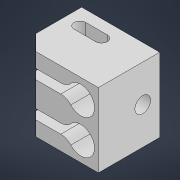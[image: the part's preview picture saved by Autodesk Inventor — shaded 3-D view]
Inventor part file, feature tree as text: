
AUTODESK INVENTOR PART (.ipt)
format: ipt  version: 2022 (Build 260153000, 153)  size: 290,304 bytes
history: native  units: in
note: dims shown in document units (in); Inventor stores cm internally (conversion verified against a paired STEP export)
features: sketch x14, extrude x8, plane x3, chamfer x3, projected_geometry x3, mirror x1
ambient origin geometry x8: Origin, YZ Plane, XZ Plane, XY Plane, X Axis, Y Axis, Z Axis, Center Point
bodies: Solid5 (feature_tree)
feature tree (32):
  plane  "Work Plane1"
  plane  "Work Plane2"
  sketch  "Sketch12"  dims[d38=0.1378in]
  extrude  "Extrusion15"  Depth=0.6693in TaperAngle=0.0deg
  extrude  "Extrusion16"  Depth=0.0984in TaperAngle=0.0deg
  chamfer  "Chamfer1"  Distance=0.2756in
  chamfer  "Chamfer2"  Distance=0.3937in
  extrude  "Extrusion18"  Depth=0.0787in
  chamfer  "Chamfer4"  Distance=0.3937in
  plane  "Work Plane3"
  extrude  "Extrusion19"  Depth=0.0787in TaperAngle=45.0deg
  mirror  "Mirror1"
  extrude  "Extrusion20"  Depth=0.0787in TaperAngle=45.0deg
  extrude  "Extrusion22"  Depth=0.0787in TaperAngle=45.0deg
  extrude  "Extrusion23"  Depth=0.0787in
  extrude  "Extrusion24"  Depth=0.3937in TaperAngle=0.0deg
  sketch  "Sketch1"  dims[d0=1.2997in d1=0.6693in d2=0.0in]
  sketch  "Sketch2"  dims[d3=0.2756in d4=0.0in d5=0.0984in d6=0.0in d7=0.2756in d8=-0.0in]
  sketch  "Sketch3"  dims[d9=0.7579in d12=0.3937in d13=0.0in]
  sketch  "Sketch4"  dims[d14=0.0984in d15=0.2362in d16=0.1575in d17=0.0787in d18=90.0deg d19=0.315in d20=0.8108in]
  sketch  "Sketch6"  dims[d28=0.1181in d29=0.2362in d30=0.1575in d31=0.0787in d32=90.0deg d33=0.315in d34=0.8108in d35=0.0984in]
  sketch  "Sketch7"  dims[d36=0.0984in]
  sketch  "Sketch9"  dims[d37=0.1378in]
  sketch  "Sketch14"  dims[d44=0.7874in d45=0.3937in d46=0.0in]
  projected_geometry  "Projected Loop2"
  sketch  "Sketch15"  dims[d47=0.3937in d48=0.0in d49=0.0787in d50=0.0787in d51=45.0deg]
  sketch  "Sketch16"  dims[d52=0.0984in d53=0.0787in d54=0.0787in d55=45.0deg]
  projected_geometry  "Projected Loop3"
  sketch  "Sketch18"  dims[d58=0.0546in d59=0.0in d63=0.1575in d64=0.0787in d65=45.0deg]
  sketch  "Sketch19"  dims[d66=0.1181in d67=0.0787in]
  projected_geometry  "Projected Loop4"
  sketch  "Sketch20"  dims[d68=-0.126in d69=0.3937in d70=0.0in d71=0.126in d72=0.5906in d73=0.0in d78=0.1575in d79=0.2244in d80=0.0in d81=0.1181in d82=0.2505in d83=0.0in d85=0.2505in d86=0.0in d84=0.0059in d87=32.2835in d88=0.0295in d89=46.4567in d90=0.0025in d91=0.0295in d92=0.0148in]
